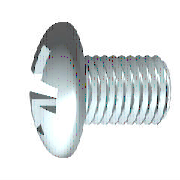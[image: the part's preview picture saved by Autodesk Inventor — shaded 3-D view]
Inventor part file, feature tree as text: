
AUTODESK INVENTOR PART (.ipt)
format: ipt  version: 2025 (Build 290162010, 162A)  size: 271,872 bytes
history: native  units: mm (DEFAULTED — no unit token found)
features: extrude x1, other x1, plane x1
ambient origin geometry x7: Origin, YZ Plane, XZ Plane, X Axis, Y Axis, Z Axis, Center Point
bodies: Solid1 (feature_tree), Body (feature_tree)
feature tree (3):
  extrude  "Slot"  Depth=2.5mm
  other  "Cut"
  plane  "Work Plane3"
